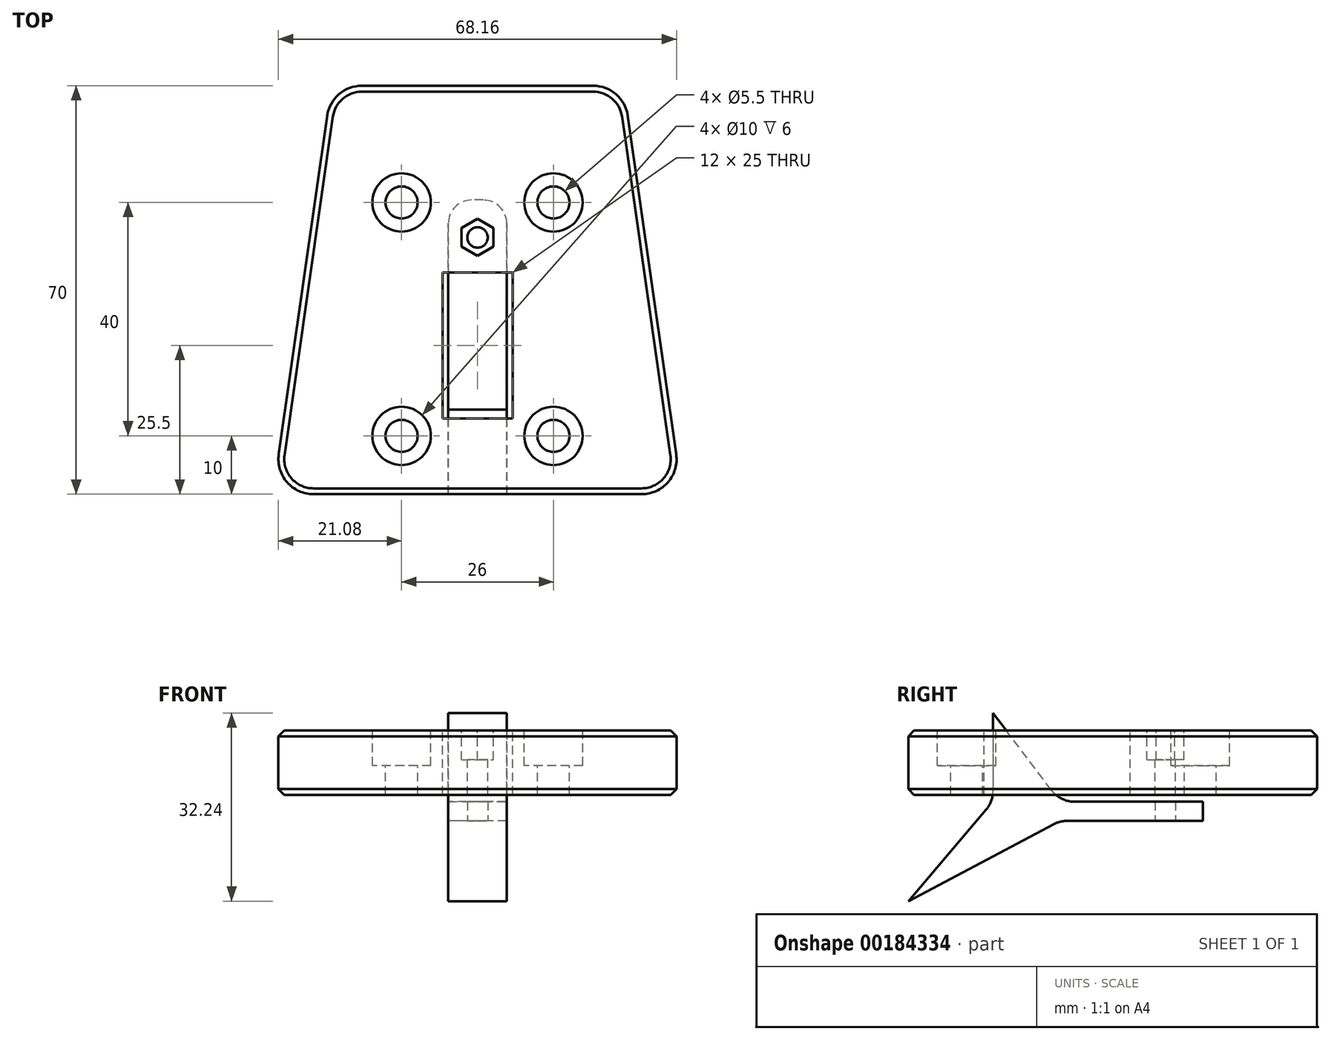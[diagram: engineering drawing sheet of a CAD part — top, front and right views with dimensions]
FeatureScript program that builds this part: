
annotation { "Feature Type Name" : "Feature", "Feature Type Description" : "" }
export const myFeature = defineFeature(function(context is Context, id is Id, definition is map)
    precondition{}
    {
        {
            var Q0;
            Q0=qCreatedBy(makeId("Top.planeOp"),FACE);
            var sketch = newSketch(context, id + "F0", { "sketchPlane" : qUnion([Q0])});
            skLineSegment(sketch, "E0", {"start": v(-28.08, 0) * mm, "end": v(28.08, 0) * mm});
            skLineSegment(sketch, "E1", {"start": v(34.02, 6.85) * mm, "end": v(25.74, 64.85) * mm});
            skLineSegment(sketch, "E2", {"start": v(19.8, 70) * mm, "end": v(-19.8, 70) * mm});
            skLineSegment(sketch, "E3", {"start": v(-25.74, 64.85) * mm, "end": v(-34.02, 6.85) * mm});
            skPoint(sketch, "E4.visualSharp", {"position": v(-25, 70) * mm});
            skArc(sketch, "E4.filletArc", {"start": v(-19.8, 70) * mm, "mid": v(-23.73, 68.53) * mm, "end": v(-25.74, 64.85) * mm});
            skPoint(sketch, "E5.visualSharp", {"position": v(25, 70) * mm});
            skArc(sketch, "E5.filletArc", {"start": v(25.74, 64.85) * mm, "mid": v(23.73, 68.53) * mm, "end": v(19.8, 70) * mm});
            skPoint(sketch, "E6.visualSharp", {"position": v(35, 0) * mm});
            skArc(sketch, "E6.filletArc", {"start": v(28.08, 0) * mm, "mid": v(32.61, 2.07) * mm, "end": v(34.02, 6.85) * mm});
            skPoint(sketch, "E7.visualSharp", {"position": v(-35, 0) * mm});
            skArc(sketch, "E7.filletArc", {"start": v(-34.02, 6.85) * mm, "mid": v(-32.61, 2.07) * mm, "end": v(-28.08, 0) * mm});
            skLineSegment(sketch, "E8.bottom", {"start": v(6, 38) * mm, "end": v(-6, 38) * mm});
            skLineSegment(sketch, "E8.top", {"start": v(6, 13) * mm, "end": v(-6, 13) * mm});
            skLineSegment(sketch, "E8.left", {"start": v(6, 38) * mm, "end": v(6, 13) * mm});
            skLineSegment(sketch, "E8.right", {"start": v(-6, 38) * mm, "end": v(-6, 13) * mm});
            skPoint(sketch, "E8.middle", {"position": v(0, 25.5) * mm});
            skCircle(sketch, "E9", {"center": v(-13, 50) * mm, "radius": 2.75 * mm});
            skCircle(sketch, "E10", {"center": v(-13, 50) * mm, "radius": 5 * mm});
            skCircle(sketch, "E11.0.1.0", {"center": v(-13, 10) * mm, "radius": 5 * mm});
            skCircle(sketch, "E11.0.1.1", {"center": v(-13, 10) * mm, "radius": 2.75 * mm});
            skCircle(sketch, "E11.1.0.0", {"center": v(13, 50) * mm, "radius": 5 * mm});
            skCircle(sketch, "E11.1.0.1", {"center": v(13, 50) * mm, "radius": 2.75 * mm});
            skCircle(sketch, "E11.1.1.0", {"center": v(13, 10) * mm, "radius": 5 * mm});
            skCircle(sketch, "E11.1.1.1", {"center": v(13, 10) * mm, "radius": 2.75 * mm});
            skLineSegment(sketch, "E11.direction1", {"start": v(-13, 50) * mm, "end": v(13, 50) * mm, "construction": true});
            skLineSegment(sketch, "E11.direction2", {"start": v(-13, 50) * mm, "end": v(-13, 10) * mm, "construction": true});
            skCircle(sketch, "E12", {"center": v(0, 44) * mm, "radius": 1.75 * mm});
            skPoint(sketch, "E12.centerSnap0", {"position": v(0, 38) * mm});
            skSolve(sketch);
        }
        {
            var Q0;
            Q0=makeQuery(id+"F0.imprint","IMPRINT",FACE,{"disambiguationData":[TD([[makeQuery(id+"F0.imprint","IMPRINT",EDGE,{"derivedFrom":sQuery(id+"F0.wireOp",EDGE,"E0")}),1.0]])]});
            var Q1;
            Q1=makeQuery(id+"F0.imprint","IMPRINT",FACE,{"disambiguationData":[TD([[makeQuery(id+"F0.imprint","IMPRINT",EDGE,{"derivedFrom":sQuery(id+"F0.wireOp",EDGE,"E11.1.0.0")}),1.0]])]});
            var Q2;
            Q2=makeQuery(id+"F0.imprint","IMPRINT",FACE,{"disambiguationData":[TD([[makeQuery(id+"F0.imprint","IMPRINT",EDGE,{"derivedFrom":sQuery(id+"F0.wireOp",EDGE,"E11.1.1.0")}),1.0]])]});
            var Q3;
            Q3=makeQuery(id+"F0.imprint","IMPRINT",FACE,{"disambiguationData":[TD([[makeQuery(id+"F0.imprint","IMPRINT",EDGE,{"derivedFrom":sQuery(id+"F0.wireOp",EDGE,"E11.0.1.0")}),1.0]])]});
            var Q4;
            Q4=makeQuery(id+"F0.imprint","IMPRINT",FACE,{"disambiguationData":[TD([[makeQuery(id+"F0.imprint","IMPRINT",EDGE,{"derivedFrom":sQuery(id+"F0.wireOp",EDGE,"E9")}),-1.0]])]});
            var Q5;
            Q5=makeQuery(id+"F0.imprint","IMPRINT",FACE,{"disambiguationData":[TD([[makeQuery(id+"F0.imprint","IMPRINT",EDGE,{"derivedFrom":sQuery(id+"F0.wireOp",EDGE,"E12")}),-1.0]])]});
            extrude(context, id + "F1", {"entities" : qUnion([Q0, Q1, Q2, Q3, Q4, Q5]), "oppositeDirection" : true, "depth" : 11 * mm});
        }
        {
            var Q0;
            Q0=makeQuery(id+"F1.opExtrude","CAP_EDGE",EDGE,{"disambiguationData":[OSD([sQuery(id+"F0.wireOp",EDGE,"E1")])],"isStart":true});
            chamfer(context, id + "F2", {"entities" : qUnion([Q0]), "width" : 1 * mm, "tangentPropagation" : true});
        }
        {
            var Q0;
            Q0=makeQuery(id+"F1.opExtrude","CAP_EDGE",EDGE,{"disambiguationData":[OSD([sQuery(id+"F0.wireOp",EDGE,"E3")])],"isStart":false});
            chamfer(context, id + "F3", {"entities" : qUnion([Q0]), "width" : 1 * mm, "tangentPropagation" : true});
        }
        {
            var Q0;
            Q0=makeQuery(id+"F0.imprint","IMPRINT",FACE,{"disambiguationData":[TD([[makeQuery(id+"F0.imprint","IMPRINT",EDGE,{"derivedFrom":sQuery(id+"F0.wireOp",EDGE,"E9")}),-1.0]])]});
            var Q1;
            Q1=makeQuery(id+"F0.imprint","IMPRINT",FACE,{"disambiguationData":[TD([[makeQuery(id+"F0.imprint","IMPRINT",EDGE,{"derivedFrom":sQuery(id+"F0.wireOp",EDGE,"E11.1.0.0")}),1.0]])]});
            var Q2;
            Q2=makeQuery(id+"F0.imprint","IMPRINT",FACE,{"disambiguationData":[TD([[makeQuery(id+"F0.imprint","IMPRINT",EDGE,{"derivedFrom":sQuery(id+"F0.wireOp",EDGE,"E11.1.1.0")}),1.0]])]});
            var Q3;
            Q3=makeQuery(id+"F0.imprint","IMPRINT",FACE,{"disambiguationData":[TD([[makeQuery(id+"F0.imprint","IMPRINT",EDGE,{"derivedFrom":sQuery(id+"F0.wireOp",EDGE,"E11.0.1.0")}),1.0]])]});
            extrude(context, id + "F4", {"entities" : qUnion([Q0, Q1, Q2, Q3]), "operationType" : NewBodyOperationType.REMOVE, "oppositeDirection" : true, "depth" : 6 * mm});
        }
        {
            var Q0;
            Q0=qCreatedBy(makeId("Right.planeOp"),FACE);
            var sketch = newSketch(context, id + "F5", { "sketchPlane" : qUnion([Q0])});
            skLineSegment(sketch, "E13", {"start": v(50.41, -12.18) * mm, "end": v(28.48, -12.18) * mm});
            skLineSegment(sketch, "E14", {"start": v(24.49, -10.2) * mm, "end": v(14.5, 3.02) * mm});
            skLineSegment(sketch, "E15", {"start": v(14.5, 3.02) * mm, "end": v(14.5, -10.34) * mm});
            skLineSegment(sketch, "E16", {"start": v(13.3, -13.58) * mm, "end": v(0, -29.22) * mm});
            skLineSegment(sketch, "E17", {"start": v(0, -29.22) * mm, "end": v(24.9, -16.05) * mm});
            skLineSegment(sketch, "E18", {"start": v(27.23, -15.47) * mm, "end": v(50.41, -15.47) * mm});
            skLineSegment(sketch, "E19", {"start": v(50.41, -15.47) * mm, "end": v(50.41, -12.18) * mm});
            skPoint(sketch, "E20.visualSharp", {"position": v(26, -12.18) * mm});
            skArc(sketch, "E20.filletArc", {"start": v(24.49, -10.2) * mm, "mid": v(26.25, -11.66) * mm, "end": v(28.48, -12.18) * mm});
            skPoint(sketch, "E21.visualSharp", {"position": v(26, -15.47) * mm});
            skArc(sketch, "E21.filletArc", {"start": v(27.23, -15.47) * mm, "mid": v(26.03, -15.62) * mm, "end": v(24.9, -16.05) * mm});
            skPoint(sketch, "E22.visualSharp", {"position": v(14.5, -12.18) * mm});
            skArc(sketch, "E22.filletArc", {"start": v(13.3, -13.58) * mm, "mid": v(14.2, -12.07) * mm, "end": v(14.5, -10.34) * mm});
            skSolve(sketch);
        }
        {
            var Q0;
            Q0=makeQuery(id+"F5.imprint","IMPRINT",FACE,{"disambiguationData":[TD([[makeQuery(id+"F5.imprint","IMPRINT",EDGE,{"derivedFrom":sQuery(id+"F5.wireOp",EDGE,"E13")}),1.0]])]});
            extrude(context, id + "F6", {"entities" : qUnion([Q0]), "depth" : 10 * mm, "symmetric" : true});
        }
        {
            var Q0;
            Q0=makeQuery(id+"F6.opExtrude","SWEPT_FACE",FACE,{"disambiguationData":[OSD([sQuery(id+"F5.wireOp",EDGE,"E18")])]});
            var sketch = newSketch(context, id + "F7", { "sketchPlane" : qUnion([Q0])});
            skCircle(sketch, "E23", {"center": v(0, -44) * mm, "radius": 1.75 * mm});
            skPoint(sketch, "E23.centerSnap0", {"position": v(0, -50.41) * mm});
            skSolve(sketch);
        }
        {
            var Q0;
            Q0=makeQuery(id+"F6.opExtrude","CAP_EDGE",EDGE,{"disambiguationData":[OSD([sQuery(id+"F5.wireOp",EDGE,"E19")])],"isStart":false});
            var Q1;
            Q1=makeQuery(id+"F6.opExtrude","CAP_EDGE",EDGE,{"disambiguationData":[OSD([sQuery(id+"F5.wireOp",EDGE,"E19")])],"isStart":true});
            fillet(context, id + "F8", {"entities" : qUnion([Q0, Q1]), "radius" : 4 * mm, "tangentPropagation" : true, "allowEdgeOverflow" : false});
        }
        {
            var Q0;
            Q0 = qSketchRegion(id + "F7", true);
            var Q1;
            Q1=makeQuery(id+"F6.opExtrude","SWEPT_FACE",FACE,{"disambiguationData":[OSD([sQuery(id+"F5.wireOp",EDGE,"E13")])]});
            extrude(context, id + "F9", {"entities" : qUnion([Q0]), "operationType" : NewBodyOperationType.REMOVE, "endBound" : BoundingType.UP_TO_SURFACE, "oppositeDirection" : true, "endBoundEntityFace" : qUnion([Q1]), "depth" : 25 * mm});
        }
        {
            var Q0;
            Q0=makeQuery(id+"F1.opExtrude","CAP_FACE",FACE,{"disambiguationData":[OSD([sQuery(id+"F0.wireOp",EDGE,"E0"),sQuery(id+"F0.wireOp",EDGE,"E1"),sQuery(id+"F0.wireOp",EDGE,"E2"),sQuery(id+"F0.wireOp",EDGE,"E3"),sQuery(id+"F0.wireOp",EDGE,"E4.filletArc"),sQuery(id+"F0.wireOp",EDGE,"E5.filletArc"),sQuery(id+"F0.wireOp",EDGE,"E6.filletArc"),sQuery(id+"F0.wireOp",EDGE,"E7.filletArc"),sQuery(id+"F0.wireOp",EDGE,"E8.bottom"),sQuery(id+"F0.wireOp",EDGE,"E8.top"),sQuery(id+"F0.wireOp",EDGE,"E8.left"),sQuery(id+"F0.wireOp",EDGE,"E8.right"),sQuery(id+"F0.wireOp",EDGE,"E9"),sQuery(id+"F0.wireOp",EDGE,"E11.0.1.1"),sQuery(id+"F0.wireOp",EDGE,"E11.1.0.1"),sQuery(id+"F0.wireOp",EDGE,"E11.1.1.1"),sQuery(id+"F0.wireOp",EDGE,"E12")])],"isStart":true});
            var sketch = newSketch(context, id + "F10", { "sketchPlane" : qUnion([Q0])});
            skCircle(sketch, "E24.cCircle", {"center": v(0, 44) * mm, "radius": 2.75 * mm, "construction": true});
            skLineSegment(sketch, "E24.0", {"start": v(2.75, 45.59) * mm, "end": v(2.75, 42.41) * mm});
            skLineSegment(sketch, "E24.1", {"start": v(2.75, 42.41) * mm, "end": v(0, 40.82) * mm});
            skLineSegment(sketch, "E24.2", {"start": v(0, 40.82) * mm, "end": v(-2.75, 42.41) * mm});
            skLineSegment(sketch, "E24.3", {"start": v(-2.75, 42.41) * mm, "end": v(-2.75, 45.59) * mm});
            skLineSegment(sketch, "E24.4", {"start": v(-2.75, 45.59) * mm, "end": v(0, 47.18) * mm});
            skLineSegment(sketch, "E24.5", {"start": v(0, 47.18) * mm, "end": v(2.75, 45.59) * mm});
            skPoint(sketch, "E24.0.midPoint", {"position": v(2.75, 44) * mm});
            skSolve(sketch);
        }
        {
            var Q0;
            Q0=makeQuery(id+"F10.imprint","IMPRINT",FACE,{"disambiguationData":[TD([[makeQuery(id+"F10.imprint","IMPRINT",EDGE,{"derivedFrom":sQuery(id+"F10.wireOp",EDGE,"E24.0")}),-1.0]])]});
            extrude(context, id + "F11", {"entities" : qUnion([Q0]), "operationType" : NewBodyOperationType.REMOVE, "oppositeDirection" : true, "depth" : 5 * mm});
        }
    });
